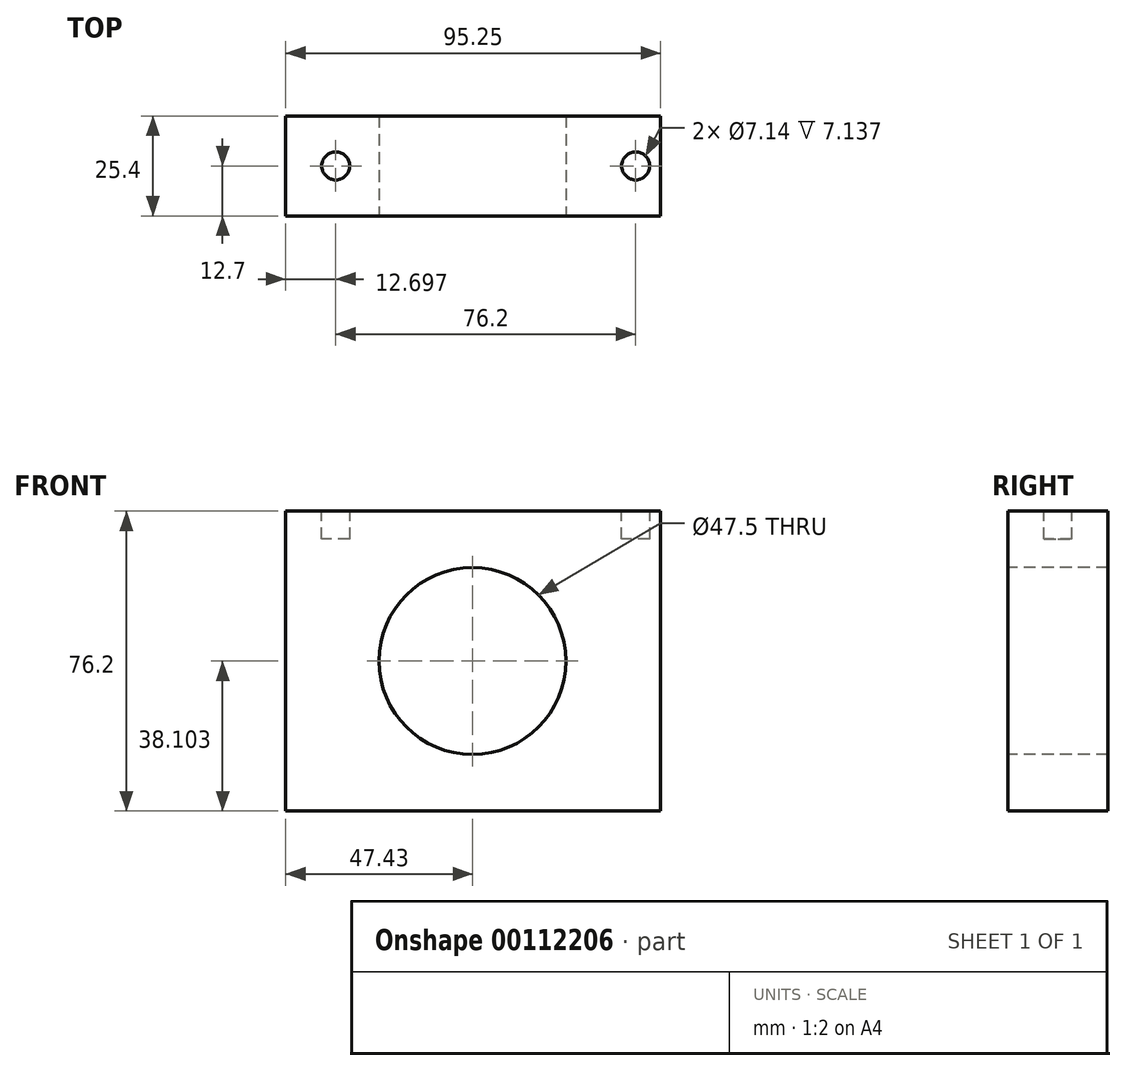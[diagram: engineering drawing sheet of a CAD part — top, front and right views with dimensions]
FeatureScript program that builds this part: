
annotation { "Feature Type Name" : "Feature", "Feature Type Description" : "" }
export const myFeature = defineFeature(function(context is Context, id is Id, definition is map)
    precondition{}
    {
        {
            var Q0;
            Q0=qCreatedBy(makeId("Front.planeOp"),FACE);
            var sketch = newSketch(context, id + "F0", { "sketchPlane" : qUnion([Q0])});
            skLineSegment(sketch, "E0.bottom", {"start": v(-47.43, 47.45) * mm, "end": v(47.82, 47.45) * mm});
            skLineSegment(sketch, "E0.top", {"start": v(-47.43, -28.75) * mm, "end": v(47.82, -28.75) * mm});
            skLineSegment(sketch, "E0.left", {"start": v(-47.43, 47.45) * mm, "end": v(-47.43, -28.75) * mm});
            skLineSegment(sketch, "E0.right", {"start": v(47.82, 47.45) * mm, "end": v(47.82, -28.75) * mm});
            skLineSegment(sketch, "E1", {"start": v(47.82, -28.75) * mm, "end": v(0.06, -28.75) * mm});
            skLineSegment(sketch, "E2", {"start": v(0.06, -28.75) * mm, "end": v(0, 9.35) * mm});
            skCircle(sketch, "E3", {"center": v(0, 9.35) * mm, "radius": 23.75 * mm});
            skSolve(sketch);
        }
        {
            var Q0;
            Q0 = qSketchRegion(id + "F0", true);
            extrude(context, id + "F1", {"entities" : qUnion([Q0]), "oppositeDirection" : true, "depth" : 25.4 * mm});
        }
        {
            var Q0;
            Q0=makeQuery(id+"F1.opExtrude","SWEPT_FACE",FACE,{"disambiguationData":[OSD([sQuery(id+"F0.wireOp",EDGE,"E0.bottom")])]});
            var sketch = newSketch(context, id + "F2", { "sketchPlane" : qUnion([Q0])});
            skLineSegment(sketch, "E4", {"start": v(-47.43, 12.7) * mm, "end": v(-34.73, 12.7) * mm});
            skCircle(sketch, "E5", {"center": v(-34.73, 12.7) * mm, "radius": 3.57 * mm});
            skLineSegment(sketch, "E6", {"start": v(-34.73, 12.7) * mm, "end": v(41.47, 12.7) * mm});
            skCircle(sketch, "E7", {"center": v(41.47, 12.7) * mm, "radius": 3.57 * mm});
            skSolve(sketch);
        }
        {
            var Q0;
            {var subQ0=sQuery(id+"F2.wireOp",EDGE,"E6");var subQ1=sQuery(id+"F2.wireOp",EDGE,"E4");var subQ2=makeQuery(id+"F2.imprint","INTERSECT",VERTEX,{"derivedFrom":[subQ1,subQ0]});Q0=makeQuery(id+"F2.imprint","IMPRINT",FACE,{"disambiguationData":[TD([[makeQuery(id+"F2.imprint","IMPRINT",EDGE,{"disambiguationData":[TD([[subQ2,1.0]])],"derivedFrom":subQ1}),1.0]])]});}
            var Q1;
            {var subQ0=sQuery(id+"F2.wireOp",EDGE,"E6");var subQ1=sQuery(id+"F2.wireOp",EDGE,"E4");var subQ2=makeQuery(id+"F2.imprint","INTERSECT",VERTEX,{"derivedFrom":[subQ1,subQ0]});Q1=makeQuery(id+"F2.imprint","IMPRINT",FACE,{"disambiguationData":[TD([[makeQuery(id+"F2.imprint","IMPRINT",EDGE,{"disambiguationData":[TD([[subQ2,1.0]])],"derivedFrom":subQ1}),-1.0]])]});}
            extrude(context, id + "F3", {"entities" : qUnion([Q0, Q1]), "operationType" : NewBodyOperationType.REMOVE, "oppositeDirection" : true, "depth" : 7.14 * mm});
        }
        {
            var Q0;
            Q0=makeQuery(id+"F1.opExtrude","SWEPT_FACE",FACE,{"disambiguationData":[OSD([sQuery(id+"F0.wireOp",EDGE,"E0.bottom")])]});
            var sketch = newSketch(context, id + "F4", { "sketchPlane" : qUnion([Q0])});
            skLineSegment(sketch, "E8", {"start": v(-34.73, 12.7) * mm, "end": v(41.47, 12.7) * mm});
            skCircle(sketch, "E9", {"center": v(41.47, 12.7) * mm, "radius": 3.57 * mm});
            skSolve(sketch);
        }
        {
            var Q0;
            Q0 = qSketchRegion(id + "F4", true);
            extrude(context, id + "F5", {"entities" : qUnion([Q0]), "operationType" : NewBodyOperationType.REMOVE, "oppositeDirection" : true, "depth" : 7.14 * mm});
        }
    });
